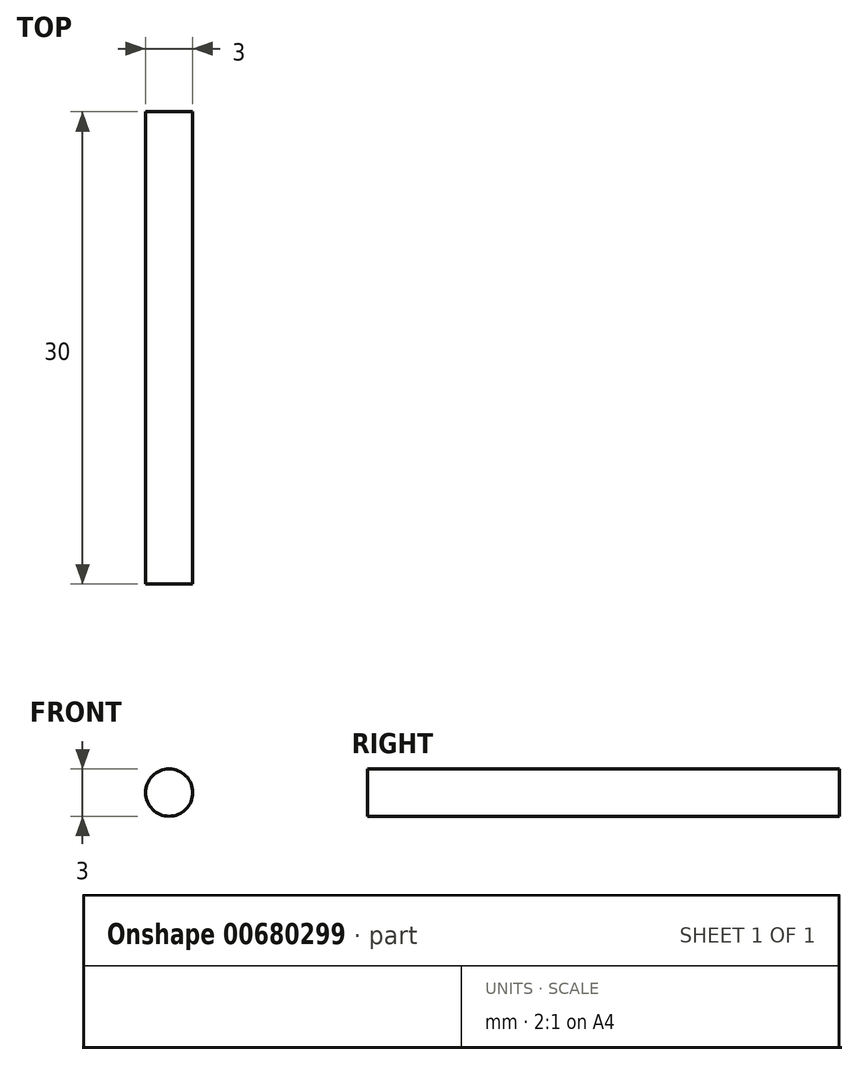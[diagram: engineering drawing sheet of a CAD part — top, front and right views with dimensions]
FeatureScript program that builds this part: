
annotation { "Feature Type Name" : "Feature", "Feature Type Description" : "" }
export const myFeature = defineFeature(function(context is Context, id is Id, definition is map)
    precondition{}
    {
        {
            var Q0;
            Q0=qCreatedBy(makeId("Front.planeOp"),FACE);
            var sketch = newSketch(context, id + "F0", { "sketchPlane" : qUnion([Q0])});
            skCircle(sketch, "E0", {"center": v(0, 0) * mm, "radius": 1.5 * mm});
            skSolve(sketch);
        }
        {
            var Q0;
            Q0 = qSketchRegion(id + "F0", true);
            extrude(context, id + "F1", {"entities" : qUnion([Q0]), "depth" : 30 * mm, "offsetDistance" : 25 * mm});
        }
    });
